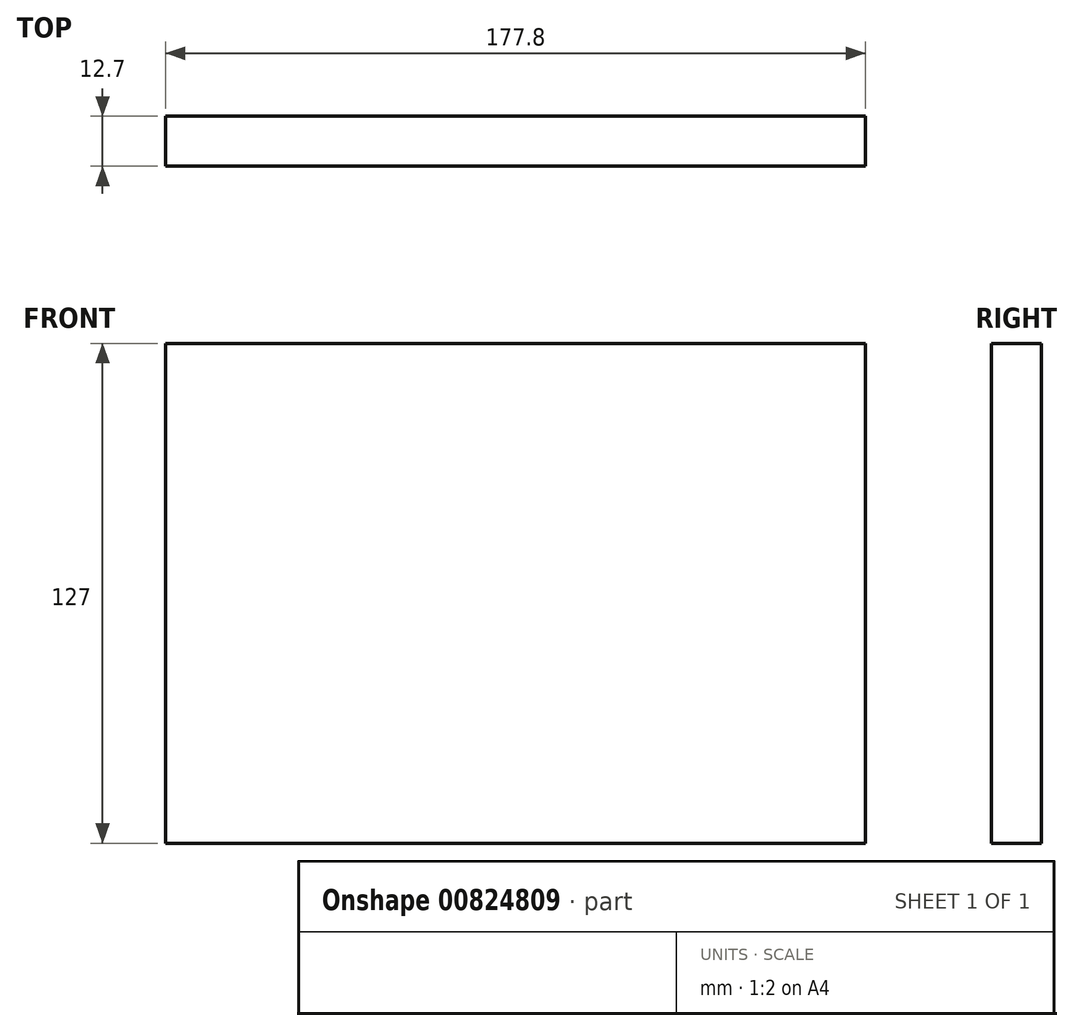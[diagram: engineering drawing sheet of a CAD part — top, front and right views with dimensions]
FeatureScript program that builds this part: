
annotation { "Feature Type Name" : "Feature", "Feature Type Description" : "" }
export const myFeature = defineFeature(function(context is Context, id is Id, definition is map)
    precondition{}
    {
        {
            var Q0;
            Q0=qCreatedBy(makeId("Front.planeOp"),FACE);
            var sketch = newSketch(context, id + "F0", { "sketchPlane" : qUnion([Q0])});
            skLineSegment(sketch, "E0.bottom", {"start": v(-87.7, 72.94) * mm, "end": v(90.1, 72.94) * mm});
            skLineSegment(sketch, "E0.top", {"start": v(-87.7, -54.06) * mm, "end": v(90.1, -54.06) * mm});
            skLineSegment(sketch, "E0.left", {"start": v(-87.7, 72.94) * mm, "end": v(-87.7, -54.06) * mm});
            skLineSegment(sketch, "E0.right", {"start": v(90.1, 72.94) * mm, "end": v(90.1, -54.06) * mm});
            skSolve(sketch);
        }
        {
            var Q0;
            Q0 = qSketchRegion(id + "F0", true);
            extrude(context, id + "F1", {"entities" : qUnion([Q0]), "depth" : 12.7 * mm, "offsetDistance" : 25 * mm});
        }
    });
